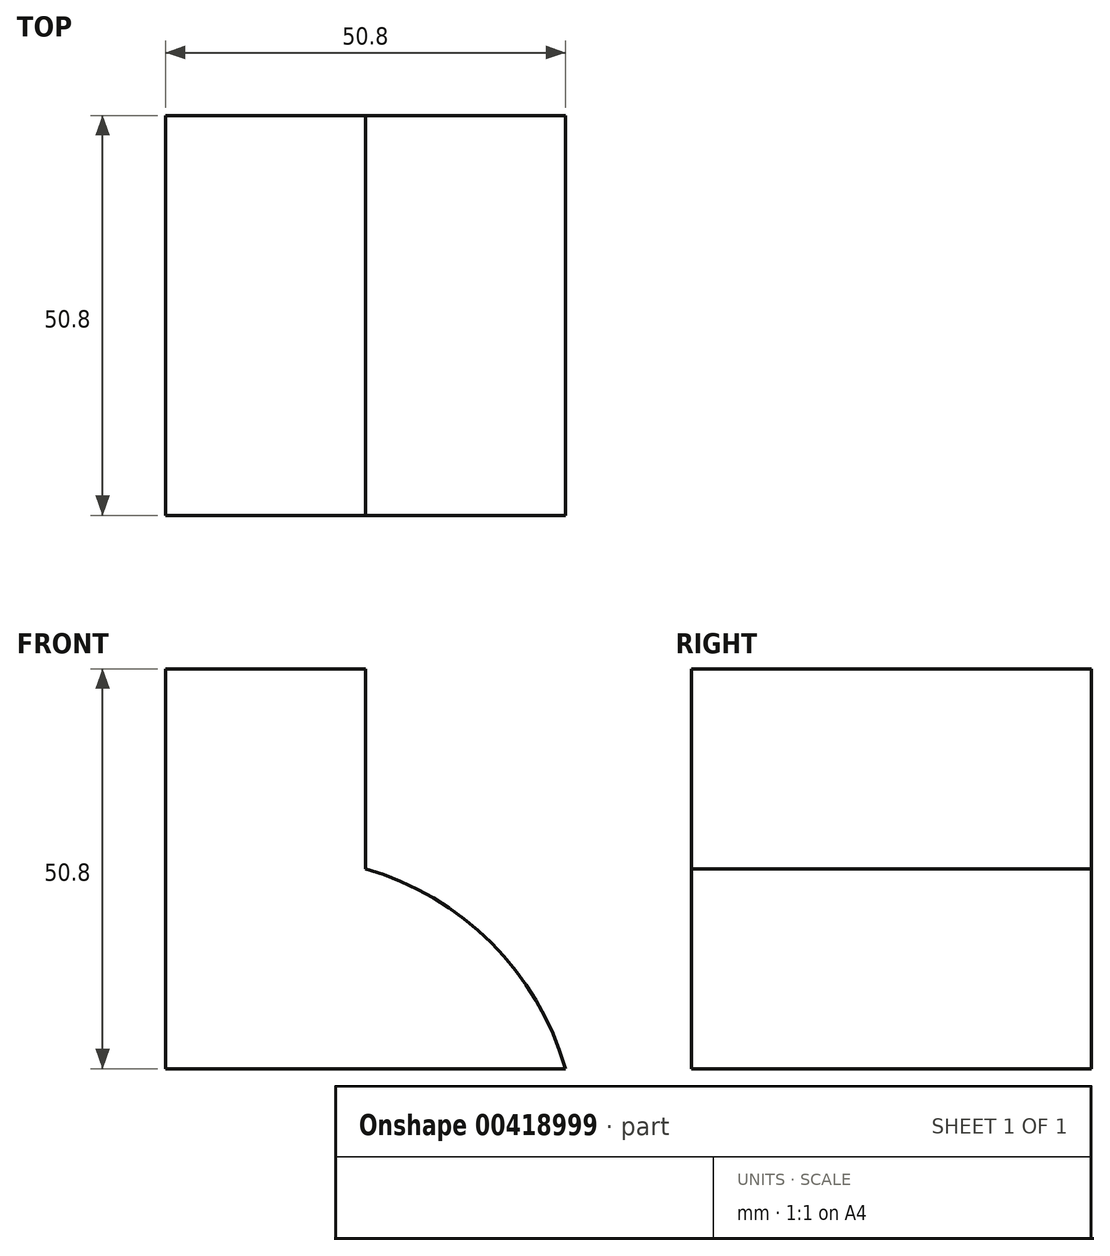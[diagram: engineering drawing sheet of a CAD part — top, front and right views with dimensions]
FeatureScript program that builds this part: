
annotation { "Feature Type Name" : "Feature", "Feature Type Description" : "" }
export const myFeature = defineFeature(function(context is Context, id is Id, definition is map)
    precondition{}
    {
        {
            var Q0;
            Q0=qCreatedBy(makeId("Front.planeOp"),FACE);
            var sketch = newSketch(context, id + "F0", { "sketchPlane" : qUnion([Q0])});
            skLineSegment(sketch, "E0", {"start": v(0, 0) * mm, "end": v(-50.8, 0) * mm});
            skLineSegment(sketch, "E1", {"start": v(-50.8, 0) * mm, "end": v(-50.8, 50.8) * mm});
            skLineSegment(sketch, "E2", {"start": v(-50.8, 50.8) * mm, "end": v(-25.4, 50.8) * mm});
            skLineSegment(sketch, "E3", {"start": v(-25.4, 50.8) * mm, "end": v(-25.4, 25.4) * mm});
            skArc(sketch, "E4", {"start": v(0, 0) * mm, "mid": v(-9.42, 15.98) * mm, "end": v(-25.4, 25.4) * mm});
            skSolve(sketch);
        }
        {
            var Q0;
            Q0=makeQuery(id+"F0.imprint","IMPRINT",FACE,{"disambiguationData":[TD([[makeQuery(id+"F0.imprint","IMPRINT",EDGE,{"derivedFrom":sQuery(id+"F0.wireOp",EDGE,"E0")}),-1.0]])]});
            extrude(context, id + "F1", {"entities" : qUnion([Q0]), "depth" : 50.8 * mm});
        }
    });
